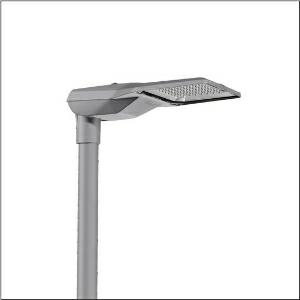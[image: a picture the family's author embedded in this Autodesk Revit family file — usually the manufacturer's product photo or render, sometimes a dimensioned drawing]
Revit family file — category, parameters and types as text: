
# Revit family: streetlight_sl_21_iq_midi___p0_8a_5xe3u31v08nb_7897
name_source: partatom
category: Lighting Fixtures
units: mm (PartAtom-declared; Revit-internal decimal feet)

## family parameters
Cut with Voids When Loaded = No
Host = Face
Light Source = No
Part Type = Normal
Room Calculation Point = No
Round Connector Dimension = Use Diameter
Shared = No

## types (1)
- --- (1 x LED, 21740 lm, 136.6 W, 3000K)
    Apparent Load = 137 VA
    CIE Flux Codes = 36 69 97 100 100
    Color Rendering = 70
    Color Temperature = 3000K
    Default Elevation = 1800 mm
    Description = Streetlight SL 21 iQ midi, mast luminaire, primary light control with lens, of PMMA, primary optical cover: cover, of toughened safety glass, transparent, light distribution: P0.8a, light emission: direct distribution, primary light characteristic: asymmetric, installation type: post-top, side-entry, LED, High Power LED, rated luminous flux: 21.740lm, luminous efficacy: 159lm/W, light colour: 730, colour temperature: 3000K, control gear: iQ-Street Remote, D4i with power reduction, control: pre-setting: logarithmic dimming characteristic, Street-Remote, Auto-Match, Temp-Guard, Lumen-Switch, Night-Set, Smart-Wire, Light-Fading, Desk-Remote (wireless, voltage-free reading and setting of iQ features in the workshop via application-optimized NFC function/RFID function), optimised constant luminous flux control (CLO 2.0), mains connection: 230..240V, AC, 50/60Hz, start of lifetime: 137W, end of service life: 144W, reduction: 61W, luminaire housing, of diecast aluminium, powder-coated, Siteco® metallic grey (DB 702S), corrosivity category C5 mid according to DIN EN ISO 12944, please order mast flange separately, inclination adjustable: 0°, 5°, 10°, 15°, sealing non-destructively replaceable, multi-level sealing system, length: 644mm, width: 335mm, height: 110mm, mast flange for spigot size: 42mm (side-entry): 5XC10008XM4, 60/48mm (side-entry/post-top): 5XC10108XM2, 76/60mm (side-entry/post-top): 5XC10108XM1, mounting height: 4..8m, Smart Interface above, protection rating (complete): IP66, insulation class (complete): insulation class II (safety insulation), certification: CE, ENEC, ENEC+, VDE, impact resistance: IK09, permissible operating ambient temperature for outdoor applications: -40..+50°C, standard-compliant lighting for roads and squares, packaging unit: 1 piece

Light Distribution: P0.8a
    Height = 111 mm
    Lamp = 1 x LED
    Lamp Light Flux = 21740 lm
    Lamp Power = 136.6 W
    Lamp count = 1
    Length = 644 mm
    Luminous efficacy = 159 lm/W
    Manufacturer = Siteco
    ModVariant = No
    Model = 5XE3U31V08NB
    Number of Poles = 1
    OnlyDefault = Yes
    Power Factor = 1
    Product Name = Streetlight SL 21 iQ midi | P0.8a
    Product group = mast luminaire | pylon top
    ProductGroupID = 6100
    Protection Class = Protection class II
    Protection Degree = IP 66
    RLX_Detail_Level = 1
    RLX_Emergency_Light_Flux = 0 lm
    RLX_Emergency_Type = 0
    RLX_Emergency_Type_DB = No
    RlxData = <blob elided: 90649 chars, md5=6ac0b41f>
    Socket = socket
    Standby Power = 0 W
    System Light Flux = 21740 lm
    System Power = 137 W
    Type Comments = factory setting: luminous flux: 100 % | dim-lin: 254 | 733 mA
    Type Image = l_1004302.jpg
    URL = http://relux.com
    VarID = @adj_068990
    Voltage = 0 V
    Weight = 0.00 kg
    Width = 336 mm

## geometry (parser evidence)
native form markers: Blend x4, Sweep x11
no freeform markers — native parametric forms only
